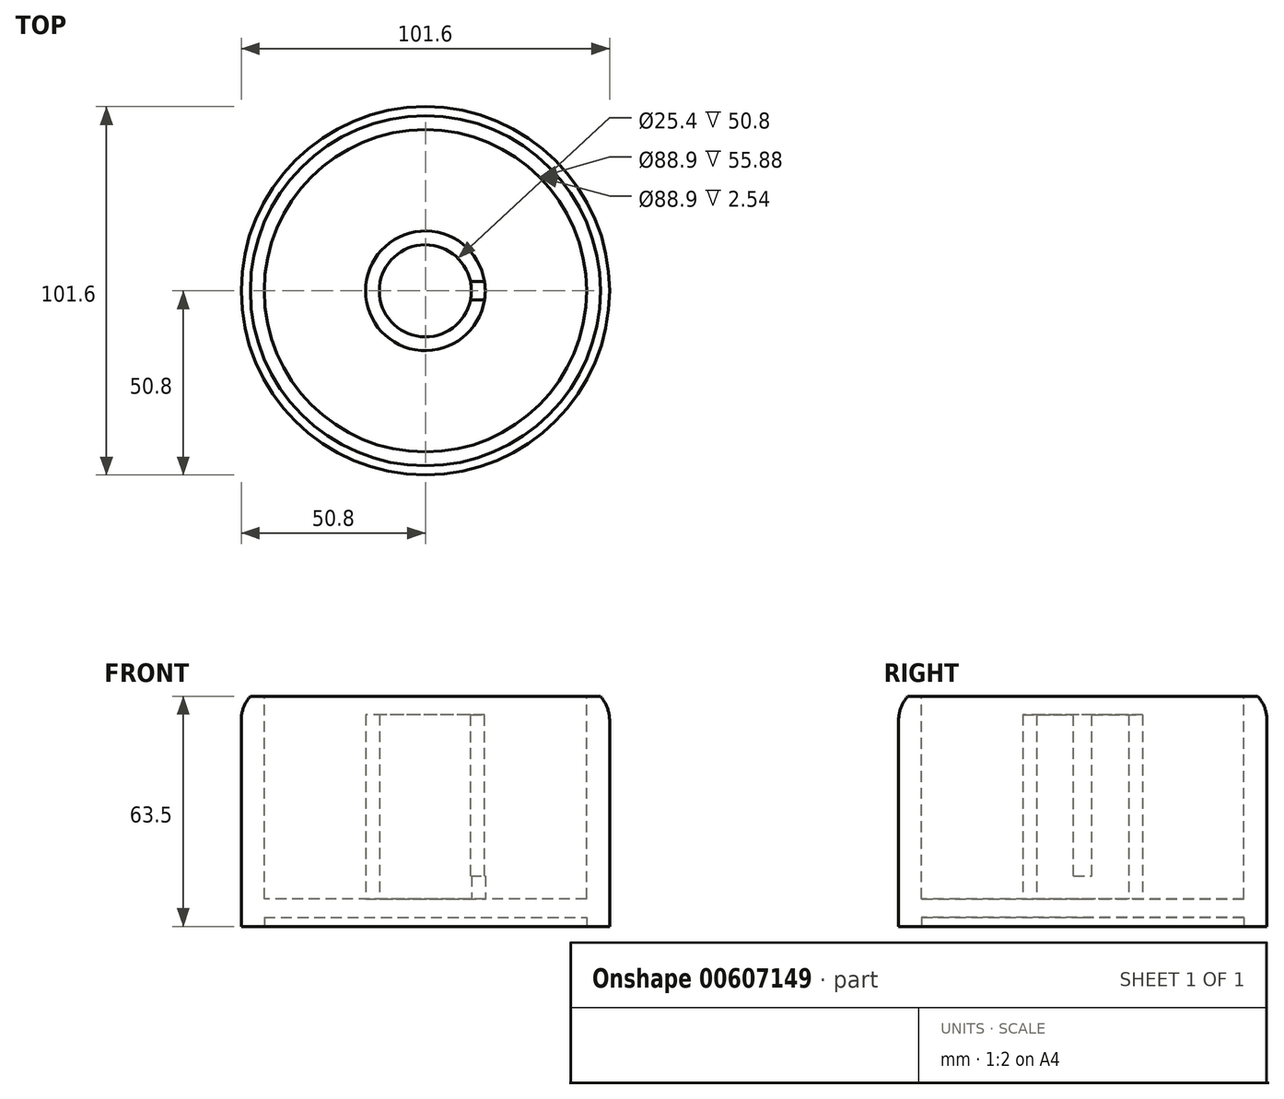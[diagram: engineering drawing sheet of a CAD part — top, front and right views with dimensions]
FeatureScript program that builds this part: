
annotation { "Feature Type Name" : "Feature", "Feature Type Description" : "" }
export const myFeature = defineFeature(function(context is Context, id is Id, definition is map)
    precondition{}
    {
        {
            var Q0;
            Q0=qCreatedBy(makeId("Top.planeOp"),FACE);
            var sketch = newSketch(context, id + "F0", { "sketchPlane" : qUnion([Q0])});
            skCircle(sketch, "E0", {"center": v(0, 0) * mm, "radius": 50.8 * mm});
            skSolve(sketch);
        }
        {
            var Q0;
            Q0=makeQuery(id+"F0.imprint","IMPRINT",FACE,{"disambiguationData":[TD([[makeQuery(id+"F0.imprint","IMPRINT",EDGE,{"derivedFrom":sQuery(id+"F0.wireOp",EDGE,"E0")}),1.0]])]});
            extrude(context, id + "F1", {"entities" : qUnion([Q0]), "depth" : 63.5 * mm, "offsetDistance" : 25.4 * mm});
        }
        {
            var Q0;
            Q0=makeQuery(id+"F1.opExtrude","CAP_FACE",FACE,{"disambiguationData":[OSD([sQuery(id+"F0.wireOp",EDGE,"E0")])],"isStart":false});
            var sketch = newSketch(context, id + "F2", { "sketchPlane" : qUnion([Q0])});
            skCircle(sketch, "E1", {"center": v(0, 0) * mm, "radius": 44.45 * mm});
            skSolve(sketch);
        }
        {
            var Q0;
            Q0=makeQuery(id+"F2.imprint","IMPRINT",FACE,{"disambiguationData":[TD([[makeQuery(id+"F2.imprint","IMPRINT",EDGE,{"derivedFrom":sQuery(id+"F2.wireOp",EDGE,"E1")}),1.0]])]});
            extrude(context, id + "F3", {"entities" : qUnion([Q0]), "operationType" : NewBodyOperationType.REMOVE, "oppositeDirection" : true, "depth" : 55.88 * mm, "offsetDistance" : 25.4 * mm});
        }
        {
            var Q0;
            Q0=makeQuery(id+"F1.opExtrude","CAP_FACE",FACE,{"disambiguationData":[OSD([sQuery(id+"F0.wireOp",EDGE,"E0")])],"isStart":true});
            var sketch = newSketch(context, id + "F4", { "sketchPlane" : qUnion([Q0])});
            skCircle(sketch, "E2", {"center": v(0, 0) * mm, "radius": 44.45 * mm});
            skSolve(sketch);
        }
        {
            var Q0;
            Q0=makeQuery(id+"F4.imprint","IMPRINT",FACE,{"disambiguationData":[TD([[makeQuery(id+"F4.imprint","IMPRINT",EDGE,{"derivedFrom":sQuery(id+"F4.wireOp",EDGE,"E2")}),1.0]])]});
            extrude(context, id + "F5", {"entities" : qUnion([Q0]), "operationType" : NewBodyOperationType.REMOVE, "oppositeDirection" : true, "depth" : 2.54 * mm, "offsetDistance" : 25.4 * mm});
        }
        {
            var Q0;
            Q0=makeQuery(id+"F1.opExtrude","CAP_EDGE",EDGE,{"disambiguationData":[OSD([sQuery(id+"F0.wireOp",EDGE,"E0")])],"isStart":false});
            chamfer(context, id + "F6", {"entities" : qUnion([Q0]), "width" : 2.54 * mm, "tangentPropagation" : true});
        }
        {
            var Q0;
            {var subQ0=sQuery(id+"F0.wireOp",EDGE,"E0");Q0=makeQuery(id+"F6.opChamfer","BLEND_EDGE",EDGE,{"blendedFrom":[makeQuery(id+"F1.opExtrude","CAP_EDGE",EDGE,{"disambiguationData":[OSD([subQ0])],"isStart":false}),makeQuery(id+"F1.opExtrude","SWEPT_FACE",FACE,{"disambiguationData":[OSD([subQ0])]})],"blendedInto":[makeQuery(id+"F1.opExtrude","SWEPT_FACE",FACE,{"disambiguationData":[OSD([subQ0])]})]});}
            fillet(context, id + "F7", {"entities" : qUnion([Q0]), "radius" : 10.16 * mm, "tangentPropagation" : true, "allowEdgeOverflow" : false});
        }
        {
            var Q0;
            Q0=makeQuery(id+"F3.boolean.opBoolean","COPY",FACE,{"derivedFrom":makeQuery(id+"F3.opExtrude","CAP_FACE",FACE,{"disambiguationData":[OSD([sQuery(id+"F2.wireOp",EDGE,"E1")])],"isStart":false})});
            var sketch = newSketch(context, id + "F8", { "sketchPlane" : qUnion([Q0])});
            skCircle(sketch, "E3", {"center": v(0, 0) * mm, "radius": 16.51 * mm});
            skCircle(sketch, "E4", {"center": v(0, 0) * mm, "radius": 12.7 * mm});
            skSolve(sketch);
        }
        {
            var Q0;
            Q0=makeQuery(id+"F8.imprint","IMPRINT",FACE,{"disambiguationData":[TD([[makeQuery(id+"F8.imprint","IMPRINT",EDGE,{"derivedFrom":sQuery(id+"F8.wireOp",EDGE,"E3")}),1.0]])]});
            extrude(context, id + "F9", {"entities" : qUnion([Q0]), "operationType" : NewBodyOperationType.ADD, "depth" : 50.8 * mm, "offsetDistance" : 25.4 * mm});
        }
        {
            var Q0;
            Q0=makeQuery(id+"F9.opExtrude","CAP_FACE",FACE,{"disambiguationData":[OSD([sQuery(id+"F8.wireOp",EDGE,"E3"),sQuery(id+"F8.wireOp",EDGE,"E4")])],"isStart":false});
            var sketch = newSketch(context, id + "F10", { "sketchPlane" : qUnion([Q0])});
            skLineSegment(sketch, "E5", {"start": v(12.7, 0) * mm, "end": v(16.51, 0) * mm});
            skLineSegment(sketch, "E6", {"start": v(14.6, 0) * mm, "end": v(14.6, 2.54) * mm});
            skLineSegment(sketch, "E7", {"start": v(14.6, 2.54) * mm, "end": v(16.31, 2.54) * mm});
            skLineSegment(sketch, "E8", {"start": v(16.31, 2.54) * mm, "end": v(12.44, 2.54) * mm});
            skLineSegment(sketch, "E9", {"start": v(14.6, 0) * mm, "end": v(14.6, -2.54) * mm});
            skLineSegment(sketch, "E10", {"start": v(14.6, -2.54) * mm, "end": v(16.31, -2.54) * mm});
            skLineSegment(sketch, "E11", {"start": v(16.31, -2.54) * mm, "end": v(12.44, -2.54) * mm});
            skSolve(sketch);
        }
        {
            var Q0;
            {var subQ3=sQuery(id+"F10.wireOp",EDGE,"E6");Q0=makeQuery(id+"F10.imprint","IMPRINT",FACE,{"disambiguationData":[TD([[makeQuery(id+"F10.imprint","IMPRINT",EDGE,{"derivedFrom":subQ3}),1.0]])]});}
            var Q1;
            {var subQ3=sQuery(id+"F10.wireOp",EDGE,"E6");Q1=makeQuery(id+"F10.imprint","IMPRINT",FACE,{"disambiguationData":[TD([[makeQuery(id+"F10.imprint","IMPRINT",EDGE,{"derivedFrom":subQ3}),-1.0]])]});}
            var Q2;
            {var subQ3=sQuery(id+"F10.wireOp",EDGE,"E9");Q2=makeQuery(id+"F10.imprint","IMPRINT",FACE,{"disambiguationData":[TD([[makeQuery(id+"F10.imprint","IMPRINT",EDGE,{"derivedFrom":subQ3}),1.0]])]});}
            var Q3;
            {var subQ3=sQuery(id+"F10.wireOp",EDGE,"E9");Q3=makeQuery(id+"F10.imprint","IMPRINT",FACE,{"disambiguationData":[TD([[makeQuery(id+"F10.imprint","IMPRINT",EDGE,{"derivedFrom":subQ3}),-1.0]])]});}
            extrude(context, id + "F11", {"entities" : qUnion([Q0, Q1, Q2, Q3]), "operationType" : NewBodyOperationType.REMOVE, "oppositeDirection" : true, "depth" : 44.45 * mm, "offsetDistance" : 25.4 * mm});
        }
    });
